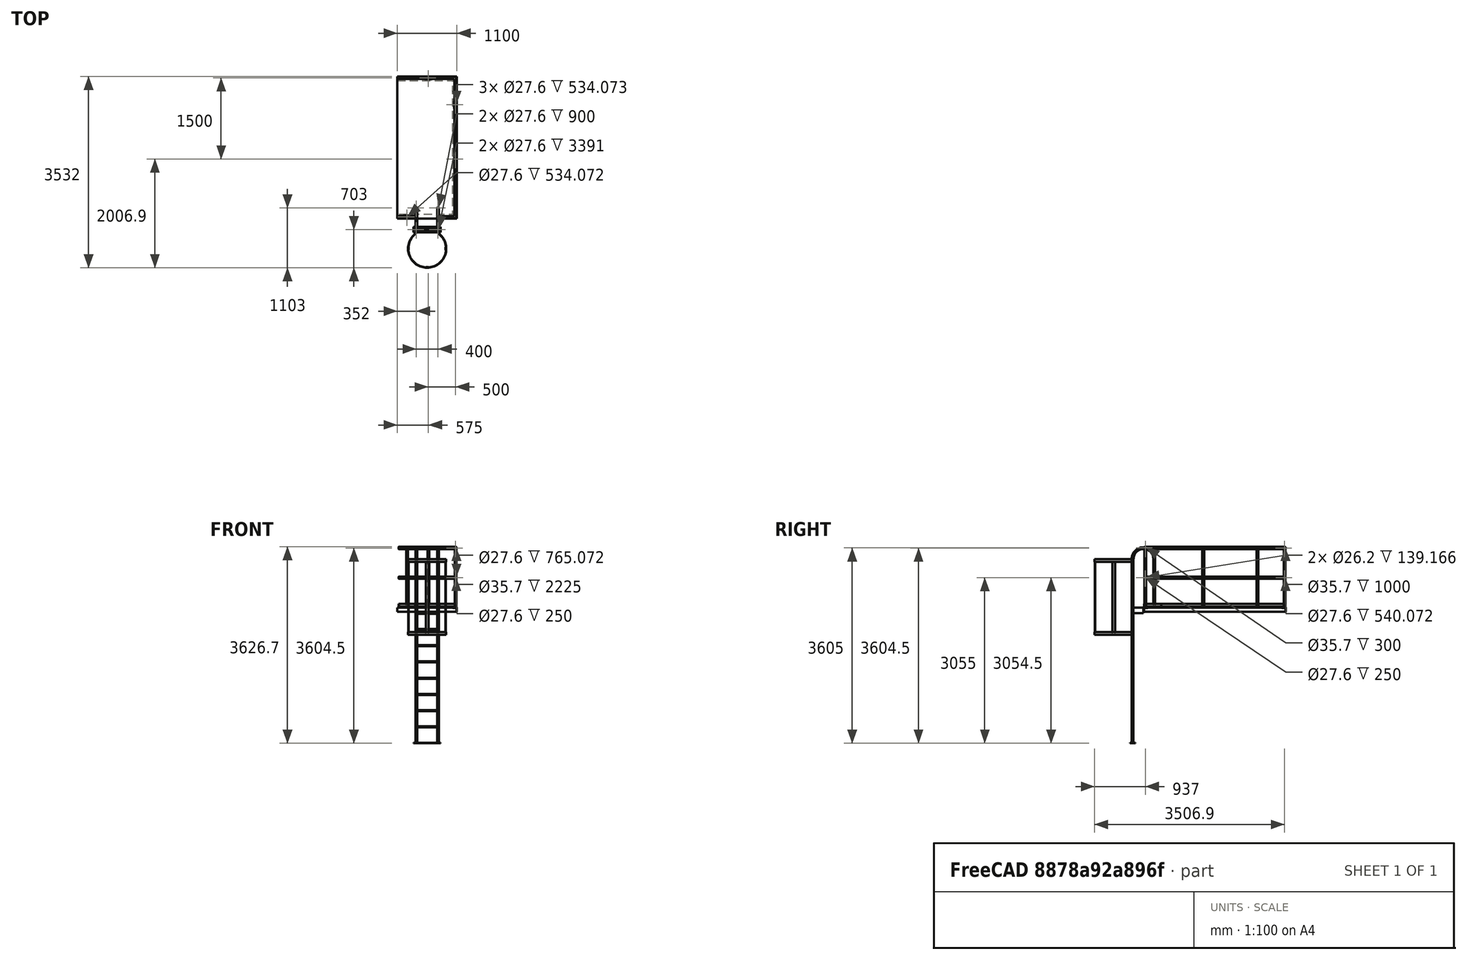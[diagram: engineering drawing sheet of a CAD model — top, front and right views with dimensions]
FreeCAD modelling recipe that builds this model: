
FCSTD DOCUMENT  (FreeCAD 1.0R39319 (Git))
Label: trestle05
License: All rights reserved
objects: Part::FeaturePython×8, Spreadsheet::Sheet×1, Part::Part2DObjectPython×1, Part::Extrusion×1, App::Part×1
note: 10 computed .brp shape members not serialized (recipe doc carries the construction recipe); baked Part::Feature solids carry a one-line shape summary decoded from their .brp

FEATURE [Spreadsheet::Sheet] Spreadsheet
  cells = A1(key)='05; A2='W; B2(W0)=1100; A3='L; B3(L0)=2700; A4='H; B4(H0)=2500
FEATURE [Part::Part2DObjectPython] Rectangle  # Draft 2D object (typed FeaturePython)
  Area = 2887500
  ChamferSize = 0
  Columns = 1
  FilletRadius = 0
  Height = 2625
  Length = 1100
  MakeFace = true
  Placement = pos=(0,0,2500) rot=(0,0,1;0rad)
  Rows = 1
  expr: .Placement.Base.z = Spreadsheet.H0
  expr: Height = Spreadsheet.L0 - 75
  expr: Length = Spreadsheet.W0
FEATURE [Part::Extrusion] Extrude
  Base = -> Rectangle
  Dir = (0,0,1)
  DirMode = 2
  FaceMakerClass = Part::FaceMakerBullseye
  FaceMakerMode = 3
  LengthFwd = 4.5
  LengthRev = 0
  Solid = false
  Symmetric = false
FEATURE [Part::FeaturePython] AngleSteel  # WARN: FeaturePython — macro-defined, semantics opaque (R4)
  A = 75
  B = 75
  L = 2625
  Placement = pos=(37.5,6.57e-13,2462.5) rot=(0,-1,0;4.71239rad)
  Solid = true
  Standard = L=2925
  g0 = 7.85
  mass = 17.9818
  size = 10
  standard = SS_Equal
  t = 6
  expr: .Placement.Base.z = Spreadsheet.H0 - 37.5
  expr: L = Spreadsheet.L0 - 75
FEATURE [Part::FeaturePython] Clone001  label="AngleSteel002"  # Draft clone (typed FeaturePython)
  AttacherType = Attacher::AttachEngine3D
  Fuse = false
  Objects = -> [AngleSteel]
  Placement = pos=(1062.5,7.34e-13,2462.5) rot=(0,1,0;3.14159rad)
  Scale = (1,1,1)
  expr: .Placement.Base.x = Spreadsheet.W0 - 37.5
  expr: .Placement.Base.z = Spreadsheet.H0 - 37.5
FEATURE [Part::FeaturePython] Corner  # WARN: FeaturePython — macro-defined, semantics opaque (R4)
  Placement = pos=(775,25,2504.5) rot=(0,0,1;0rad)
  Reverse = false
  Standard = L1=700.0,L2=300.0
  g0 = 7.85
  h = 1100
  k = 90
  l1 = 300
  l2 = 300
  mass = 4.65222
  p = 1000
  spec = 0
  type = 2
  expr: .Placement.Base.z = Spreadsheet.H0 + 4.5
  expr: l1 = Spreadsheet.W0 - 800
FEATURE [Part::FeaturePython] Corner001  # WARN: FeaturePython — macro-defined, semantics opaque (R4)
  Placement = pos=(1075,324.9,2504.5) rot=(0,0,1;1.5708rad)
  Reverse = false
  Standard = L1=2575.0,L2=1450.0
  g0 = 7.85
  h = 1100
  k = 90
  l1 = 2275
  l2 = 1050
  mass = 35.6516
  p = 1000
  spec = 0
  type = 2
  expr: .Placement.Base.x = Spreadsheet.W0 - 25
  expr: .Placement.Base.z = Spreadsheet.H0 + 4.5
  expr: l1 = Spreadsheet.L0 - 425
  expr: l2 = Spreadsheet.W0 - 50
FEATURE [Part::FeaturePython] LadderA_with_cage  # WARN: FeaturePython — macro-defined, semantics opaque (R4)
  FloorHeight = 2500
  Placement = pos=(752,-204,0) rot=(0,0,1;1.5708rad)
  RailingHeight = 1100
  StepHeight = 300
  g0 = 7.85
  mass = 55.6527
  type = 1
  expr: FloorHeight = Spreadsheet.H0
FEATURE [Part::FeaturePython] StraightLine  # WARN: FeaturePython — macro-defined, semantics opaque (R4)
  JPN = てすり
  Placement = pos=(30,30,2505) rot=(0,0,1;0rad)
  Reverse = false
  Standard = L1=300.0  L2=1500
  g0 = 7.85
  h = 1100
  l1 = 300
  mass = 5.60854
  p = 1000
  spec = 0
  type = 0
FEATURE [Part::FeaturePython] AngleSteel001  # WARN: FeaturePython — macro-defined, semantics opaque (R4)
  A = 75
  B = 75
  JPN = 等辺山形鋼
  L = 1100
  Placement = pos=(1100,37.5,2462.5) rot=(0.57735,-0.57735,-0.57735;4.18879rad)
  Solid = true
  Standard = L75x75x6  L=1000
  g0 = 7.85
  mass = 7.53523
  size = 10
  standard = SS_Equal
  t = 6
  type = 00_Angle
  expr: .Placement.Base.x = Spreadsheet.W0
  expr: .Placement.Base.z = Spreadsheet.H0 - 37.5
  expr: L = Spreadsheet.W0
FEATURE [Part::FeaturePython] AngleSteel002  label="AngleSteel003"  # WARN: FeaturePython — macro-defined, semantics opaque (R4)
  A = 75
  B = 75
  JPN = 等辺山形鋼
  L = 1100
  Placement = pos=(0,2587.5,2462.5) rot=(0.57735,0.57735,-0.57735;2.0944rad)
  Solid = true
  Standard = L75x75x6  L=1000
  g0 = 7.85
  mass = 7.53523
  size = 10
  standard = SS_Equal
  t = 6
  type = 00_Angle
  expr: .Placement.Base.y = Spreadsheet.L0 - 112.5
  expr: .Placement.Base.z = Spreadsheet.H0 - 37.5
  expr: L = Spreadsheet.W0
FEATURE [App::Part] Part  label="trestleAssy"
  Group = -> [Rectangle,Extrude,AngleSteel,Clone001,Corner,Corner001,LadderA_with_cage,StraightLine,Spreadsheet,AngleSteel001,AngleSteel002]
  Origin = -> Origin
